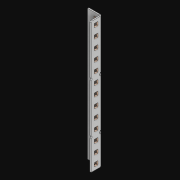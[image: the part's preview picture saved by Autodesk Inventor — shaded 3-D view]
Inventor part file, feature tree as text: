
AUTODESK INVENTOR PART (.ipt)
format: ipt  version: 2021 (Build 250183000, 183)  size: 1,144,832 bytes
history: native  units: in
note: dims shown in document units (in); Inventor stores cm internally (conversion verified against a paired STEP export)
features: extrude x28, other x26, sketch x4, pattern_linear x2, sheet_metal_op x1
ambient origin geometry x8: Origin, YZ Plane, XZ Plane, XY Plane, X Axis, Y Axis, Z Axis, Center Point
bodies: Solid1 (feature_tree)
feature tree (61):
  pattern_linear  "Rectangular Pattern1"  Spacing1=0.5in  [1 undecoded]
  pattern_linear  "Rectangular Pattern3"  Count1=13  [1 undecoded]
  extrude  "Extrusion1"  Depth=0.5in
  extrude  "Extrusion2"  Depth=0.5in
  sketch  "Sketch1"  dims[d0=0.182in]
  other  "Srf1"
  sketch  "Sketch3"  dims[d1=0.063in d2=0.0in]
  other  "Srf3"
  other  "Srf4"
  other  "Srf5"
  other  "Srf6"
  other  "Srf7"
  other  "Srf8"
  other  "Srf9"
  other  "Srf10"
  other  "Srf11"
  other  "Srf12"
  other  "Srf13"
  other  "Srf14"
  other  "Srf15"
  other  "Srf142"
  other  "Srf143"
  other  "Srf144"
  other  "Srf145"
  other  "Srf146"
  other  "Srf147"
  other  "Srf148"
  other  "Srf149"
  other  "Srf150"
  other  "Srf151"
  other  "Srf152"
  other  "Srf153"
  sketch  "Sketch4"  dims[d6=0.182in]
  sketch  "Sketch5"  dims[d7=0.063in d8=0.0in d11=0.5in d12=0.3937in d14=0.5in d18=5.1181in d20=0.5in d21=11.0in d22=0.0in d23=0.841in d24=0.0in]
  sheet_metal_op  "Fold1"
  extrude  "ExtrusionSrf1"  TaperAngle=0.0deg  [1 undecoded]
  extrude  "ExtrusionSrf3"  Depth=0.5in TaperAngle=0.0deg
  extrude  "ExtrusionSrf4"  [1 undecoded]
  extrude  "ExtrusionSrf5"  [1 undecoded]
  extrude  "ExtrusionSrf6"  [1 undecoded]
  extrude  "ExtrusionSrf7"  [1 undecoded]
  extrude  "ExtrusionSrf8"  [1 undecoded]
  extrude  "ExtrusionSrf9"  [1 undecoded]
  extrude  "ExtrusionSrf10"  [1 undecoded]
  extrude  "ExtrusionSrf11"  [1 undecoded]
  extrude  "ExtrusionSrf12"  [1 undecoded]
  extrude  "ExtrusionSrf13"  [1 undecoded]
  extrude  "ExtrusionSrf14"  [1 undecoded]
  extrude  "ExtrusionSrf15"  [1 undecoded]
  extrude  "ExtrusionSrf142"  [1 undecoded]
  extrude  "ExtrusionSrf143"  [1 undecoded]
  extrude  "ExtrusionSrf144"  [1 undecoded]
  extrude  "ExtrusionSrf145"  [1 undecoded]
  extrude  "ExtrusionSrf146"  [1 undecoded]
  extrude  "ExtrusionSrf147"  [1 undecoded]
  extrude  "ExtrusionSrf148"  [1 undecoded]
  extrude  "ExtrusionSrf149"  [1 undecoded]
  extrude  "ExtrusionSrf150"  [1 undecoded]
  extrude  "ExtrusionSrf151"  [1 undecoded]
  extrude  "ExtrusionSrf152"  [1 undecoded]
  extrude  "ExtrusionSrf153"  [1 undecoded]
note: 27 required parameter values undecoded (feature->parameter linkage not recoverable at this tier; creation-order binding heuristic only, values carry confidence <= 0.55)
